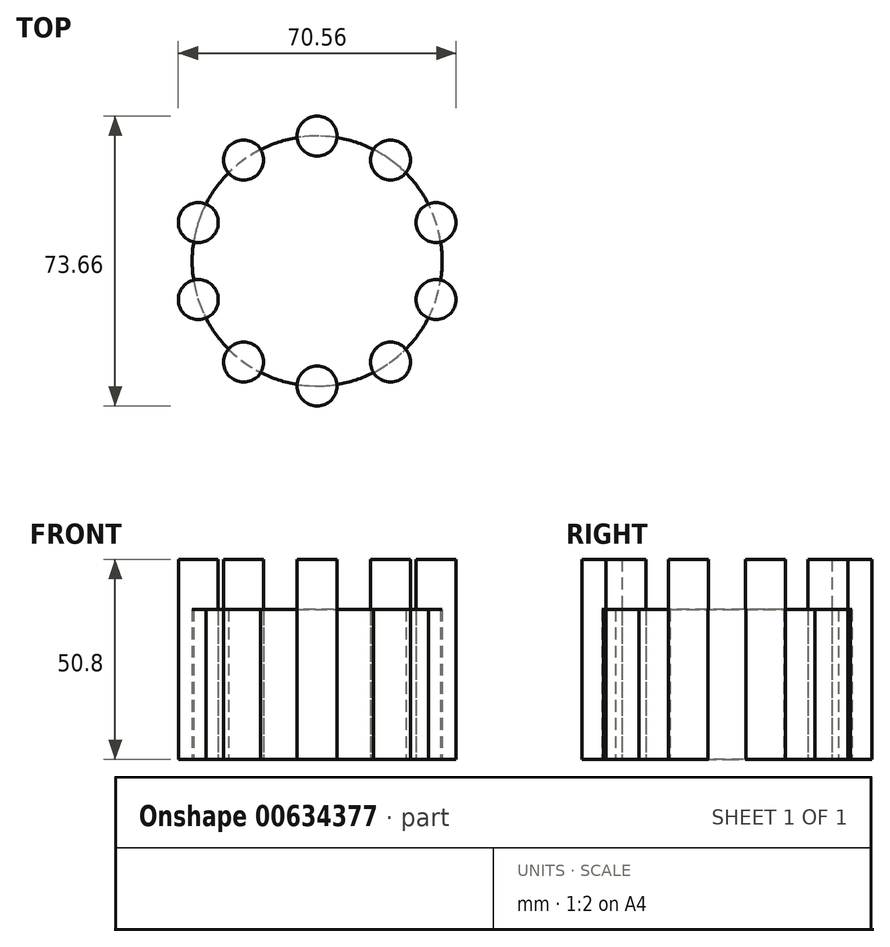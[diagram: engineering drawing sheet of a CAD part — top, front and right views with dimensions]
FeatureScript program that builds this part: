
annotation { "Feature Type Name" : "Feature", "Feature Type Description" : "" }
export const myFeature = defineFeature(function(context is Context, id is Id, definition is map)
    precondition{}
    {
        {
            var Q0;
            Q0=qCreatedBy(makeId("Top.planeOp"),FACE);
            var sketch = newSketch(context, id + "F0", { "sketchPlane" : qUnion([Q0])});
            skCircle(sketch, "E0", {"center": v(0, 0) * mm, "radius": 31.75 * mm});
            skSolve(sketch);
        }
        {
            var Q0;
            Q0=qSketchRegion(id+"F0",true);
            extrude(context, id + "F1", {"entities" : qUnion([Q0]), "depth" : 38.1 * mm});
        }
        {
            var Q0;
            Q0=qCreatedBy(makeId("Top.planeOp"),FACE);
            var sketch = newSketch(context, id + "F2", { "sketchPlane" : qUnion([Q0])});
            skCircle(sketch, "E1", {"center": v(0, 31.75) * mm, "radius": 5.08 * mm});
            skCircle(sketch, "E2.1.0", {"center": v(-18.66, 25.69) * mm, "radius": 5.08 * mm});
            skCircle(sketch, "E2.2.0", {"center": v(-30.2, 9.81) * mm, "radius": 5.08 * mm});
            skCircle(sketch, "E2.3.0", {"center": v(-30.2, -9.81) * mm, "radius": 5.08 * mm});
            skCircle(sketch, "E2.4.0", {"center": v(-18.66, -25.69) * mm, "radius": 5.08 * mm});
            skCircle(sketch, "E2.5.0", {"center": v(0, -31.75) * mm, "radius": 5.08 * mm});
            skCircle(sketch, "E2.6.0", {"center": v(18.66, -25.69) * mm, "radius": 5.08 * mm});
            skCircle(sketch, "E2.7.0", {"center": v(30.2, -9.81) * mm, "radius": 5.08 * mm});
            skCircle(sketch, "E2.8.0", {"center": v(30.2, 9.81) * mm, "radius": 5.08 * mm});
            skCircle(sketch, "E2.9.0", {"center": v(18.66, 25.69) * mm, "radius": 5.08 * mm});
            skPoint(sketch, "E2.center", {"position": v(0, 0) * mm});
            skSolve(sketch);
        }
        {
            var Q0;
            Q0=qSketchRegion(id+"F2",true);
            extrude(context, id + "F3", {"entities" : qUnion([Q0]), "depth" : 50.8 * mm});
        }
        {
            var Q0;
            Q0=makeQuery(id+"F1.opExtrude","SWEPT_BODY",BODY,{"disambiguationData":[OSD([sQuery(id+"F0.wireOp",EDGE,"E0")])]});
            var Q1;
            Q1=makeQuery(id+"F3.opExtrude","SWEPT_BODY",BODY,{"disambiguationData":[OSD([sQuery(id+"F2.wireOp",EDGE,"E1")])]});
            var Q2;
            Q2=makeQuery(id+"F3.opExtrude","SWEPT_BODY",BODY,{"disambiguationData":[OSD([sQuery(id+"F2.wireOp",EDGE,"E2.1.0")])]});
            var Q3;
            Q3=makeQuery(id+"F3.opExtrude","SWEPT_BODY",BODY,{"disambiguationData":[OSD([sQuery(id+"F2.wireOp",EDGE,"E2.2.0")])]});
            var Q4;
            Q4=makeQuery(id+"F3.opExtrude","SWEPT_BODY",BODY,{"disambiguationData":[OSD([sQuery(id+"F2.wireOp",EDGE,"E2.3.0")])]});
            var Q5;
            Q5=makeQuery(id+"F3.opExtrude","SWEPT_BODY",BODY,{"disambiguationData":[OSD([sQuery(id+"F2.wireOp",EDGE,"E2.4.0")])]});
            var Q6;
            Q6=makeQuery(id+"F3.opExtrude","SWEPT_BODY",BODY,{"disambiguationData":[OSD([sQuery(id+"F2.wireOp",EDGE,"E2.5.0")])]});
            var Q7;
            Q7=makeQuery(id+"F3.opExtrude","SWEPT_BODY",BODY,{"disambiguationData":[OSD([sQuery(id+"F2.wireOp",EDGE,"E2.6.0")])]});
            var Q8;
            Q8=makeQuery(id+"F3.opExtrude","SWEPT_BODY",BODY,{"disambiguationData":[OSD([sQuery(id+"F2.wireOp",EDGE,"E2.7.0")])]});
            var Q9;
            Q9=makeQuery(id+"F3.opExtrude","SWEPT_BODY",BODY,{"disambiguationData":[OSD([sQuery(id+"F2.wireOp",EDGE,"E2.8.0")])]});
            var Q10;
            Q10=makeQuery(id+"F3.opExtrude","SWEPT_BODY",BODY,{"disambiguationData":[OSD([sQuery(id+"F2.wireOp",EDGE,"E2.9.0")])]});
            booleanBodies(context, id + "F4", {"operationType" : BooleanOperationType.INTERSECTION, "tools" : qUnion([Q0, Q1, Q2, Q3, Q4, Q5, Q6, Q7, Q8, Q9, Q10]), "keepTools" : true});
        }
        {
            var Q0;
            Q0=makeQuery(id+"F3.opExtrude","SWEPT_BODY",BODY,{"disambiguationData":[OSD([sQuery(id+"F2.wireOp",EDGE,"E2.4.0")])]});
            var Q1;
            Q1=makeQuery(id+"F1.opExtrude","SWEPT_BODY",BODY,{"disambiguationData":[OSD([sQuery(id+"F0.wireOp",EDGE,"E0")])]});
            booleanBodies(context, id + "F5", {"operationType" : BooleanOperationType.INTERSECTION, "tools" : qUnion([Q0, Q1]), "keepTools" : true});
        }
        {
            var Q0;
            Q0=makeQuery(id+"F3.opExtrude","SWEPT_BODY",BODY,{"disambiguationData":[OSD([sQuery(id+"F2.wireOp",EDGE,"E2.3.0")])]});
            var Q1;
            Q1=makeQuery(id+"F1.opExtrude","SWEPT_BODY",BODY,{"disambiguationData":[OSD([sQuery(id+"F0.wireOp",EDGE,"E0")])]});
            booleanBodies(context, id + "F6", {"operationType" : BooleanOperationType.INTERSECTION, "tools" : qUnion([Q0, Q1]), "keepTools" : true});
        }
        {
            var Q0;
            Q0=makeQuery(id+"F3.opExtrude","SWEPT_BODY",BODY,{"disambiguationData":[OSD([sQuery(id+"F2.wireOp",EDGE,"E2.2.0")])]});
            var Q1;
            Q1=makeQuery(id+"F1.opExtrude","SWEPT_BODY",BODY,{"disambiguationData":[OSD([sQuery(id+"F0.wireOp",EDGE,"E0")])]});
            booleanBodies(context, id + "F7", {"operationType" : BooleanOperationType.INTERSECTION, "tools" : qUnion([Q0, Q1]), "keepTools" : true});
        }
        {
            var Q0;
            Q0=makeQuery(id+"F3.opExtrude","SWEPT_BODY",BODY,{"disambiguationData":[OSD([sQuery(id+"F2.wireOp",EDGE,"E2.1.0")])]});
            var Q1;
            Q1=makeQuery(id+"F1.opExtrude","SWEPT_BODY",BODY,{"disambiguationData":[OSD([sQuery(id+"F0.wireOp",EDGE,"E0")])]});
            booleanBodies(context, id + "F8", {"operationType" : BooleanOperationType.INTERSECTION, "tools" : qUnion([Q0, Q1]), "keepTools" : true});
        }
        {
            var Q0;
            Q0=makeQuery(id+"F3.opExtrude","SWEPT_BODY",BODY,{"disambiguationData":[OSD([sQuery(id+"F2.wireOp",EDGE,"E1")])]});
            var Q1;
            Q1=makeQuery(id+"F1.opExtrude","SWEPT_BODY",BODY,{"disambiguationData":[OSD([sQuery(id+"F0.wireOp",EDGE,"E0")])]});
            booleanBodies(context, id + "F9", {"operationType" : BooleanOperationType.INTERSECTION, "tools" : qUnion([Q0, Q1]), "keepTools" : true});
        }
        {
            var Q0;
            Q0=makeQuery(id+"F3.opExtrude","SWEPT_BODY",BODY,{"disambiguationData":[OSD([sQuery(id+"F2.wireOp",EDGE,"E2.9.0")])]});
            var Q1;
            Q1=makeQuery(id+"F1.opExtrude","SWEPT_BODY",BODY,{"disambiguationData":[OSD([sQuery(id+"F0.wireOp",EDGE,"E0")])]});
            booleanBodies(context, id + "F10", {"operationType" : BooleanOperationType.INTERSECTION, "tools" : qUnion([Q0, Q1]), "keepTools" : true});
        }
        {
            var Q0;
            Q0=makeQuery(id+"F3.opExtrude","SWEPT_BODY",BODY,{"disambiguationData":[OSD([sQuery(id+"F2.wireOp",EDGE,"E2.8.0")])]});
            var Q1;
            Q1=makeQuery(id+"F1.opExtrude","SWEPT_BODY",BODY,{"disambiguationData":[OSD([sQuery(id+"F0.wireOp",EDGE,"E0")])]});
            booleanBodies(context, id + "F11", {"operationType" : BooleanOperationType.INTERSECTION, "tools" : qUnion([Q0, Q1]), "keepTools" : true});
        }
        {
            var Q0;
            Q0=makeQuery(id+"F3.opExtrude","SWEPT_BODY",BODY,{"disambiguationData":[OSD([sQuery(id+"F2.wireOp",EDGE,"E2.7.0")])]});
            var Q1;
            Q1=makeQuery(id+"F1.opExtrude","SWEPT_BODY",BODY,{"disambiguationData":[OSD([sQuery(id+"F0.wireOp",EDGE,"E0")])]});
            booleanBodies(context, id + "F12", {"operationType" : BooleanOperationType.INTERSECTION, "tools" : qUnion([Q0, Q1]), "keepTools" : true});
        }
        {
            var Q0;
            Q0=makeQuery(id+"F3.opExtrude","SWEPT_BODY",BODY,{"disambiguationData":[OSD([sQuery(id+"F2.wireOp",EDGE,"E2.6.0")])]});
            var Q1;
            Q1=makeQuery(id+"F1.opExtrude","SWEPT_BODY",BODY,{"disambiguationData":[OSD([sQuery(id+"F0.wireOp",EDGE,"E0")])]});
            booleanBodies(context, id + "F13", {"operationType" : BooleanOperationType.INTERSECTION, "tools" : qUnion([Q0, Q1]), "keepTools" : true});
        }
        {
            var Q0;
            Q0=makeQuery(id+"F3.opExtrude","SWEPT_BODY",BODY,{"disambiguationData":[OSD([sQuery(id+"F2.wireOp",EDGE,"E2.5.0")])]});
            var Q1;
            Q1=makeQuery(id+"F1.opExtrude","SWEPT_BODY",BODY,{"disambiguationData":[OSD([sQuery(id+"F0.wireOp",EDGE,"E0")])]});
            booleanBodies(context, id + "F14", {"operationType" : BooleanOperationType.INTERSECTION, "tools" : qUnion([Q0, Q1]), "keepTools" : true});
        }
    });
